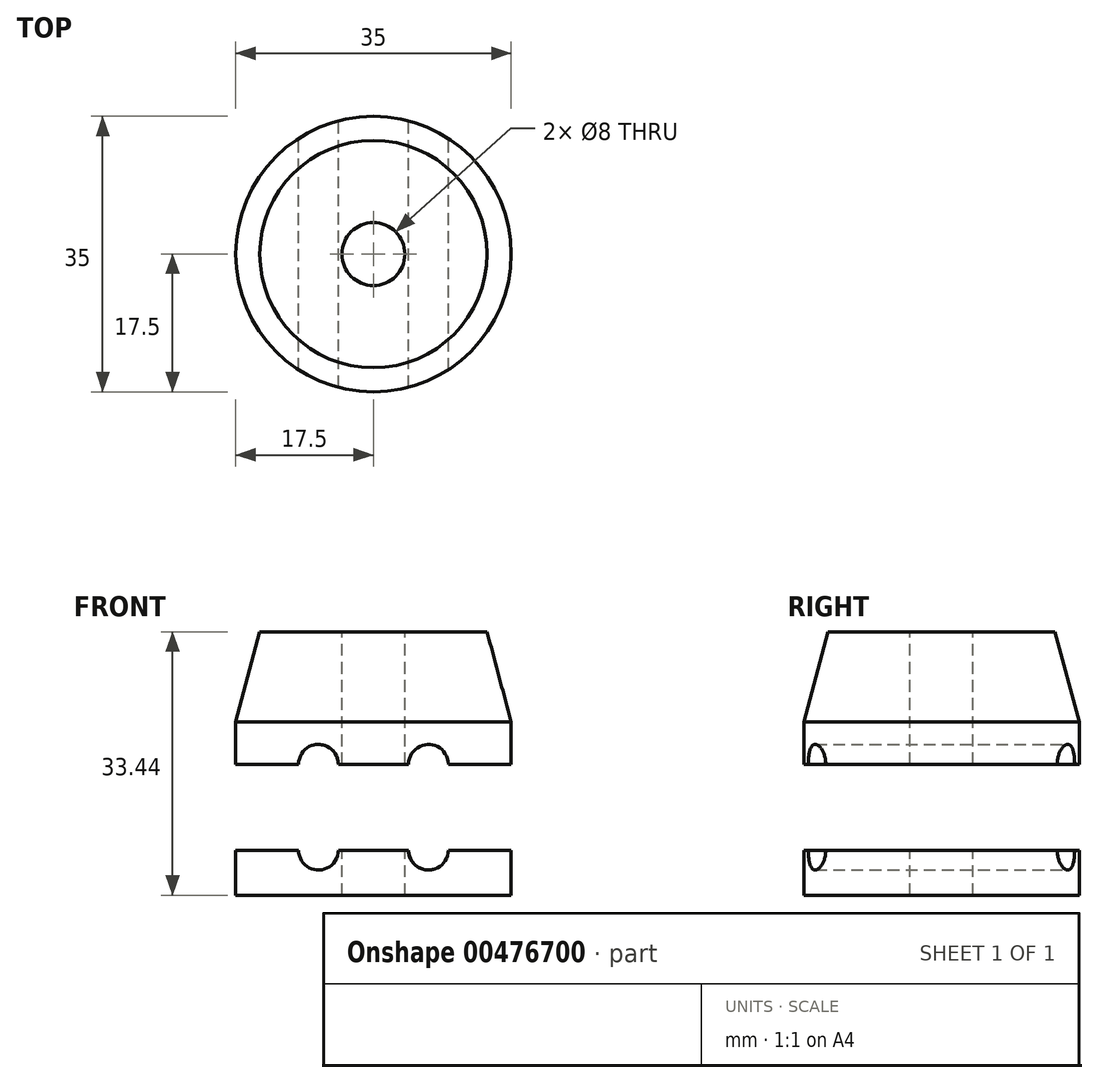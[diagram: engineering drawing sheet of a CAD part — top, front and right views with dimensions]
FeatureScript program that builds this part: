
annotation { "Feature Type Name" : "Feature", "Feature Type Description" : "" }
export const myFeature = defineFeature(function(context is Context, id is Id, definition is map)
    precondition{}
    {
        {
            var Q0;
            Q0=qCreatedBy(makeId("Front.planeOp"),FACE);
            var sketch = newSketch(context, id + "F0", { "sketchPlane" : qUnion([Q0])});
            skLineSegment(sketch, "E0", {"start": v(0, 0) * mm, "end": v(0, 11.43) * mm});
            skLineSegment(sketch, "E1.bottom", {"start": v(0, 11.43) * mm, "end": v(14.44, 11.43) * mm});
            skLineSegment(sketch, "E1.top", {"start": v(0, 0) * mm, "end": v(17.5, 0) * mm});
            skLineSegment(sketch, "E1.left", {"start": v(0, 11.43) * mm, "end": v(0, 0) * mm});
            skLineSegment(sketch, "E2.top", {"start": v(0, -5.38) * mm, "end": v(17.5, -5.38) * mm});
            skLineSegment(sketch, "E2.left", {"start": v(0, 0) * mm, "end": v(0, -5.38) * mm});
            skLineSegment(sketch, "E2.right", {"start": v(17.5, 0) * mm, "end": v(17.5, -5.38) * mm});
            skLineSegment(sketch, "E3", {"start": v(17.5, 0) * mm, "end": v(14.44, 11.43) * mm});
            skLineSegment(sketch, "E4.bottom", {"start": v(0, -5.38) * mm, "end": v(17.5, -5.38) * mm, "construction": true});
            skLineSegment(sketch, "E5.bottom", {"start": v(0, -16.3) * mm, "end": v(17.5, -16.3) * mm});
            skLineSegment(sketch, "E5.top", {"start": v(0, -22) * mm, "end": v(17.5, -22) * mm});
            skLineSegment(sketch, "E5.left", {"start": v(0, -16.3) * mm, "end": v(0, -22) * mm});
            skLineSegment(sketch, "E5.right", {"start": v(17.5, -16.3) * mm, "end": v(17.5, -22) * mm});
            skLineSegment(sketch, "E6", {"start": v(6.99, -25.21) * mm, "end": v(6.99, -16.3) * mm});
            skLineSegment(sketch, "E7.MirrorCS", {"start": v(0, -5.38) * mm, "end": v(-17.5, -5.38) * mm});
            skLineSegment(sketch, "E8.MirrorCS", {"start": v(0, -22) * mm, "end": v(-17.5, -22) * mm});
            skLineSegment(sketch, "E9.MirrorCS", {"start": v(0, -16.3) * mm, "end": v(-17.5, -16.3) * mm});
            skLineSegment(sketch, "E10.MirrorCS", {"start": v(-6.98, -25.21) * mm, "end": v(-6.99, -16.3) * mm});
            skLineSegment(sketch, "E11.MirrorCS", {"start": v(-17.5, 0) * mm, "end": v(-14.44, 11.43) * mm});
            skLineSegment(sketch, "E12.MirrorCS", {"start": v(-17.5, 0) * mm, "end": v(-17.5, -5.38) * mm});
            skLineSegment(sketch, "E13.MirrorCS", {"start": v(-17.5, -16.3) * mm, "end": v(-17.5, -22) * mm});
            skLineSegment(sketch, "E14.MirrorCS", {"start": v(0, 0) * mm, "end": v(-17.5, 0) * mm});
            skLineSegment(sketch, "E15.MirrorCS", {"start": v(0, 11.43) * mm, "end": v(-14.44, 11.43) * mm});
            skLineSegment(sketch, "E16.trimOffspring", {"start": v(-6.99, -5.38) * mm, "end": v(-6.99, 10.66) * mm});
            skLineSegment(sketch, "E17.trimOffspring", {"start": v(6.98, -5.38) * mm, "end": v(6.98, 10.66) * mm});
            skSolve(sketch);
        }
        {
            var Q0;
            {var subQ0=sQuery(id+"F0.wireOp",EDGE,"E1.left");Q0=makeQuery(id+"F0.imprint","IMPRINT",FACE,{"disambiguationData":[TD([[makeQuery(id+"F0.imprint","IMPRINT",EDGE,{"derivedFrom":subQ0}),1.0]])]});}
            var Q1;
            {var subQ0=sQuery(id+"F0.wireOp",EDGE,"E3");Q1=makeQuery(id+"F0.imprint","IMPRINT",FACE,{"disambiguationData":[TD([[makeQuery(id+"F0.imprint","IMPRINT",EDGE,{"derivedFrom":subQ0}),1.0]])]});}
            var Q2;
            {var subQ0=sQuery(id+"F0.wireOp",EDGE,"E2.right");Q2=makeQuery(id+"F0.imprint","IMPRINT",FACE,{"disambiguationData":[TD([[makeQuery(id+"F0.imprint","IMPRINT",EDGE,{"derivedFrom":subQ0}),-1.0]])]});}
            var Q3;
            {var subQ0=sQuery(id+"F0.wireOp",EDGE,"E2.left");Q3=makeQuery(id+"F0.imprint","IMPRINT",FACE,{"disambiguationData":[TD([[makeQuery(id+"F0.imprint","IMPRINT",EDGE,{"derivedFrom":subQ0}),1.0]])]});}
            var Q4;
            {var subQ0=sQuery(id+"F0.wireOp",EDGE,"E5.left");Q4=makeQuery(id+"F0.imprint","IMPRINT",FACE,{"disambiguationData":[TD([[makeQuery(id+"F0.imprint","IMPRINT",EDGE,{"derivedFrom":subQ0}),1.0]])]});}
            var Q5;
            {var subQ0=sQuery(id+"F0.wireOp",EDGE,"E5.right");Q5=makeQuery(id+"F0.imprint","IMPRINT",FACE,{"disambiguationData":[TD([[makeQuery(id+"F0.imprint","IMPRINT",EDGE,{"derivedFrom":subQ0}),-1.0]])]});}
            var Q6;
            Q6=sQuery(id+"F0.wireOp",EDGE,"E1.left");
            revolve(context, id + "F1", {"entities" : qUnion([Q0, Q1, Q2, Q3, Q4, Q5]), "axis" : qUnion([Q6]), "revolveType" : RevolveType.FULL});
        }
        {
            var Q0;
            Q0=sQuery(id+"F0.wireOp",VERTEX,"E17.trimOffspring.start");
            var Q1;
            Q1=sQuery(id+"F0.wireOp",VERTEX,"E16.trimOffspring.start");
            var Q2;
            Q2=sQuery(id+"F0.wireOp",VERTEX,"E6.end");
            var Q3;
            Q3=sQuery(id+"F0.wireOp",VERTEX,"E10.MirrorCS.end");
            var Q4;
            Q4=makeQuery(id+"F1.opRevolve","SWEPT_BODY",BODY,{"disambiguationData":[OSD([sQuery(id+"F0.wireOp",EDGE,"E1.bottom"),sQuery(id+"F0.wireOp",EDGE,"E2.top"),sQuery(id+"F0.wireOp",EDGE,"E2.right"),sQuery(id+"F0.wireOp",EDGE,"E3"),sQuery(id+"F0.wireOp",EDGE,"E1.left"),sQuery(id+"F0.wireOp",EDGE,"E2.left")])]});
            var Q5;
            Q5=makeQuery(id+"F1.opRevolve","SWEPT_BODY",BODY,{"disambiguationData":[OSD([sQuery(id+"F0.wireOp",EDGE,"E5.bottom"),sQuery(id+"F0.wireOp",EDGE,"E5.top"),sQuery(id+"F0.wireOp",EDGE,"E5.right"),sQuery(id+"F0.wireOp",EDGE,"E5.left")])]});
            hole(context, id + "F2", {"style" : HoleStyle.SIMPLE, "endStyle" : HoleEndStyle.THROUGH, "oppositeDirection" : true, "holeDiameter" : 5.05 * mm, "isTappedThrough" : true, "tappedDepth" : 12.7 * mm, "tapClearance" : 3, "startFromSketch" : true, "locations" : qUnion([Q0, Q1, Q2, Q3]), "scope" : qUnion([Q4, Q5])});
        }
        {
            var Q0;
            Q0=sQuery(id+"F0.wireOp",VERTEX,"E16.trimOffspring.start");
            var Q1;
            Q1=sQuery(id+"F0.wireOp",VERTEX,"E17.trimOffspring.start");
            var Q2;
            Q2=sQuery(id+"F0.wireOp",VERTEX,"E6.end");
            var Q3;
            Q3=sQuery(id+"F0.wireOp",VERTEX,"E10.MirrorCS.end");
            var Q4;
            Q4=makeQuery(id+"F1.opRevolve","SWEPT_BODY",BODY,{"disambiguationData":[OSD([sQuery(id+"F0.wireOp",EDGE,"E1.bottom"),sQuery(id+"F0.wireOp",EDGE,"E2.top"),sQuery(id+"F0.wireOp",EDGE,"E2.right"),sQuery(id+"F0.wireOp",EDGE,"E3"),sQuery(id+"F0.wireOp",EDGE,"E1.left"),sQuery(id+"F0.wireOp",EDGE,"E2.left")])]});
            var Q5;
            Q5=makeQuery(id+"F1.opRevolve","SWEPT_BODY",BODY,{"disambiguationData":[OSD([sQuery(id+"F0.wireOp",EDGE,"E5.bottom"),sQuery(id+"F0.wireOp",EDGE,"E5.top"),sQuery(id+"F0.wireOp",EDGE,"E5.right"),sQuery(id+"F0.wireOp",EDGE,"E5.left")])]});
            hole(context, id + "F3", {"style" : HoleStyle.SIMPLE, "endStyle" : HoleEndStyle.THROUGH, "holeDiameter" : 5.05 * mm, "isTappedThrough" : true, "tappedDepth" : 12.7 * mm, "tapClearance" : 3, "startFromSketch" : true, "locations" : qUnion([Q0, Q1, Q2, Q3]), "scope" : qUnion([Q4, Q5])});
        }
        {
            var Q0;
            Q0=makeQuery(id+"F1.opRevolve","SWEPT_FACE",FACE,{"disambiguationData":[OSD([sQuery(id+"F0.wireOp",EDGE,"E1.bottom")])]});
            var sketch = newSketch(context, id + "F4", { "sketchPlane" : qUnion([Q0])});
            skCircle(sketch, "E18", {"center": v(0, 0) * mm, "radius": 4 * mm});
            skSolve(sketch);
        }
        {
            var Q0;
            Q0=sQuery(id+"F4.wireOp",VERTEX,"E18.center");
            var Q1;
            Q1=makeQuery(id+"F1.opRevolve","SWEPT_BODY",BODY,{"disambiguationData":[OSD([sQuery(id+"F0.wireOp",EDGE,"E1.bottom"),sQuery(id+"F0.wireOp",EDGE,"E2.top"),sQuery(id+"F0.wireOp",EDGE,"E2.right"),sQuery(id+"F0.wireOp",EDGE,"E3"),sQuery(id+"F0.wireOp",EDGE,"E1.left"),sQuery(id+"F0.wireOp",EDGE,"E2.left")])]});
            var Q2;
            Q2=makeQuery(id+"F1.opRevolve","SWEPT_BODY",BODY,{"disambiguationData":[OSD([sQuery(id+"F0.wireOp",EDGE,"E5.bottom"),sQuery(id+"F0.wireOp",EDGE,"E5.top"),sQuery(id+"F0.wireOp",EDGE,"E5.right"),sQuery(id+"F0.wireOp",EDGE,"E5.left")])]});
            hole(context, id + "F5", {"style" : HoleStyle.SIMPLE, "endStyle" : HoleEndStyle.THROUGH, "holeDiameter" : 8 * mm, "isTappedThrough" : true, "tappedDepth" : 12.7 * mm, "tapClearance" : 3, "startFromSketch" : true, "locations" : qUnion([Q0]), "scope" : qUnion([Q1, Q2])});
        }
    });
